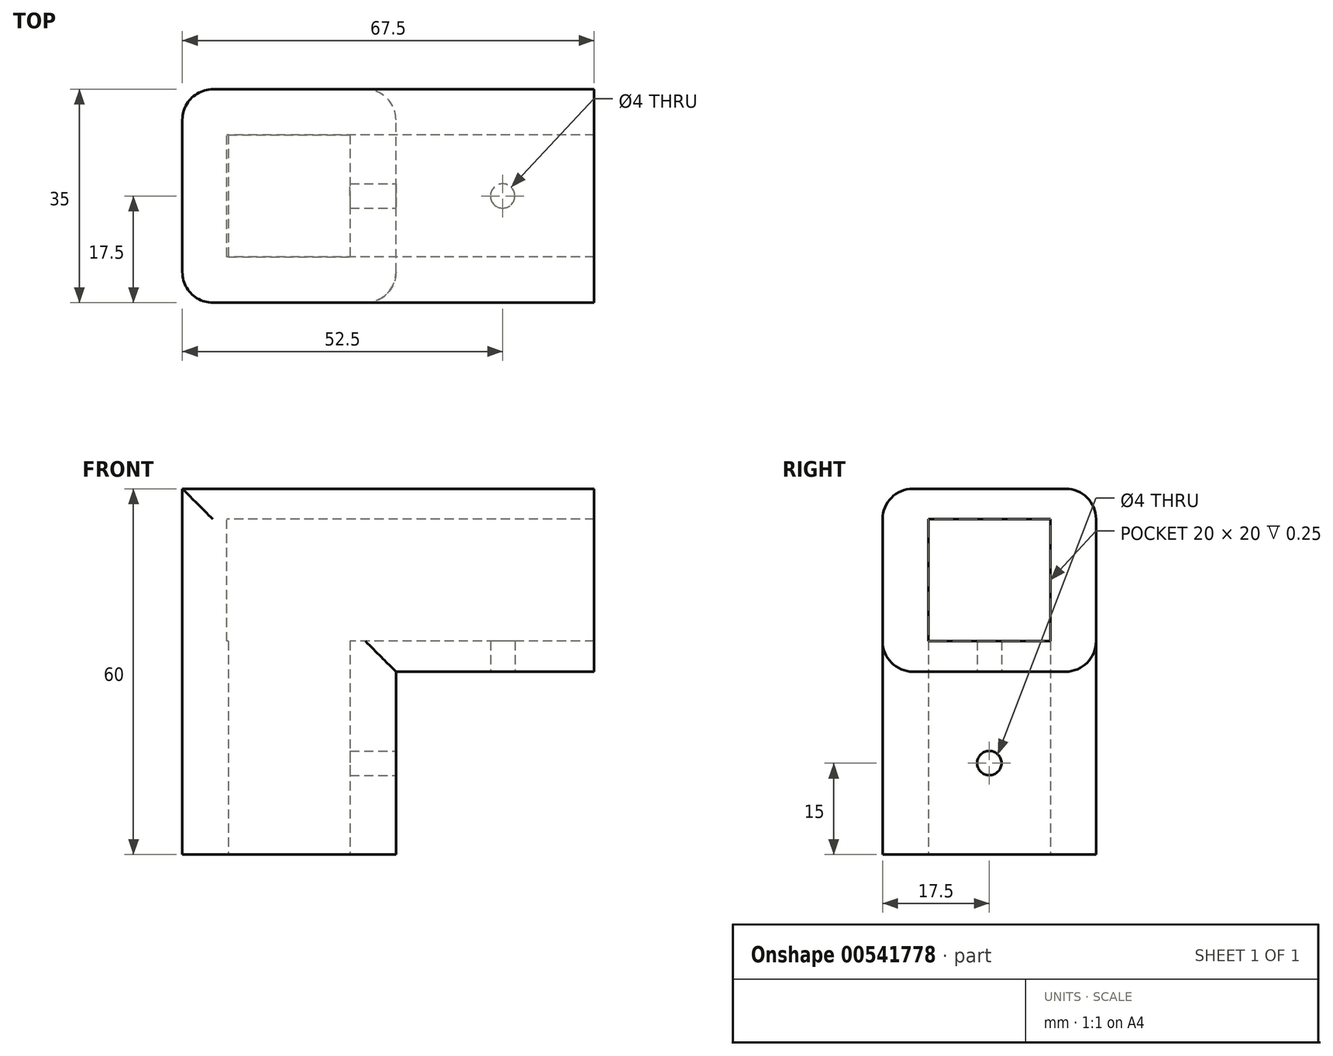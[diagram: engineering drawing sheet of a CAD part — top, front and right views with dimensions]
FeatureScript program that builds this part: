
annotation { "Feature Type Name" : "Feature", "Feature Type Description" : "" }
export const myFeature = defineFeature(function(context is Context, id is Id, definition is map)
    precondition{}
    {
        {
            var Q0;
            Q0=qCreatedBy(makeId("Top.planeOp"),FACE);
            var sketch = newSketch(context, id + "F0", { "sketchPlane" : qUnion([Q0])});
            skLineSegment(sketch, "E0.bottom", {"start": v(-17.5, -17.5) * mm, "end": v(17.5, -17.5) * mm});
            skLineSegment(sketch, "E0.top", {"start": v(-17.5, 17.5) * mm, "end": v(17.5, 17.5) * mm});
            skLineSegment(sketch, "E0.left", {"start": v(-17.5, -17.5) * mm, "end": v(-17.5, 17.5) * mm});
            skLineSegment(sketch, "E0.right", {"start": v(17.5, -17.5) * mm, "end": v(17.5, 17.5) * mm});
            skLineSegment(sketch, "E1.bottom", {"start": v(-10, -10) * mm, "end": v(10, -10) * mm});
            skLineSegment(sketch, "E1.top", {"start": v(-10, 10) * mm, "end": v(10, 10) * mm});
            skLineSegment(sketch, "E1.left", {"start": v(-10, -10) * mm, "end": v(-10, 10) * mm});
            skLineSegment(sketch, "E1.right", {"start": v(10, -10) * mm, "end": v(10, 10) * mm});
            skPoint(sketch, "E2", {"position": v(0, 10) * mm});
            skPoint(sketch, "E3", {"position": v(0, 17.5) * mm});
            skPoint(sketch, "E4", {"position": v(-17.5, 0) * mm});
            skPoint(sketch, "E5", {"position": v(-10, 0) * mm});
            skSolve(sketch);
        }
        {
            var Q0;
            Q0=makeQuery(id+"F0.imprint","IMPRINT",FACE,{"disambiguationData":[TD([[makeQuery(id+"F0.imprint","IMPRINT",EDGE,{"derivedFrom":sQuery(id+"F0.wireOp",EDGE,"E0.bottom")}),1.0]])]});
            extrude(context, id + "F1", {"entities" : qUnion([Q0]), "depth" : 60 * mm, "offsetDistance" : 25 * mm});
        }
        {
            var Q0;
            Q0=makeQuery(id+"F1.opExtrude","SWEPT_EDGE",EDGE,{"disambiguationData":[OSD([sQuery(id+"F0.wireOp",EDGE,"E0.top"),sQuery(id+"F0.wireOp",EDGE,"E0.right")])]});
            var Q1;
            Q1=makeQuery(id+"F1.opExtrude","SWEPT_EDGE",EDGE,{"disambiguationData":[OSD([sQuery(id+"F0.wireOp",EDGE,"E0.top"),sQuery(id+"F0.wireOp",EDGE,"E0.left")])]});
            var Q2;
            Q2=makeQuery(id+"F1.opExtrude","SWEPT_EDGE",EDGE,{"disambiguationData":[OSD([sQuery(id+"F0.wireOp",EDGE,"E0.bottom"),sQuery(id+"F0.wireOp",EDGE,"E0.right")])]});
            var Q3;
            Q3=makeQuery(id+"F1.opExtrude","SWEPT_EDGE",EDGE,{"disambiguationData":[OSD([sQuery(id+"F0.wireOp",EDGE,"E0.bottom"),sQuery(id+"F0.wireOp",EDGE,"E0.left")])]});
            fillet(context, id + "F2", {"entities" : qUnion([Q0, Q1, Q2, Q3]), "radius" : 5 * mm, "tangentPropagation" : true, "allowEdgeOverflow" : false});
        }
        {
            var Q0;
            Q0=makeQuery(id+"F1.opExtrude","SWEPT_FACE",FACE,{"disambiguationData":[OSD([sQuery(id+"F0.wireOp",EDGE,"E0.right")])]});
            var sketch = newSketch(context, id + "F3", { "sketchPlane" : qUnion([Q0])});
            skCircle(sketch, "E6", {"center": v(0, 40) * mm, "radius": 2 * mm});
            skCircle(sketch, "E7", {"center": v(0, 15) * mm, "radius": 2 * mm});
            skSolve(sketch);
        }
        {
            var Q0;
            Q0=qSketchRegion(id+"F3",true);
            extrude(context, id + "F4", {"entities" : qUnion([Q0]), "operationType" : NewBodyOperationType.REMOVE, "oppositeDirection" : true, "depth" : 10 * mm, "offsetDistance" : 25 * mm});
        }
        {
            var Q0;
            Q0=makeQuery(id+"F1.opExtrude","CAP_FACE",FACE,{"disambiguationData":[OSD([sQuery(id+"F0.wireOp",EDGE,"E0.bottom"),sQuery(id+"F0.wireOp",EDGE,"E0.top"),sQuery(id+"F0.wireOp",EDGE,"E0.left"),sQuery(id+"F0.wireOp",EDGE,"E0.right"),sQuery(id+"F0.wireOp",EDGE,"E1.bottom"),sQuery(id+"F0.wireOp",EDGE,"E1.top"),sQuery(id+"F0.wireOp",EDGE,"E1.left"),sQuery(id+"F0.wireOp",EDGE,"E1.right")])],"isStart":false});
            var sketch = newSketch(context, id + "F5", { "sketchPlane" : qUnion([Q0])});
            skLineSegment(sketch, "E8.bottom", {"start": v(-17.26, -17.5) * mm, "end": v(17.26, -17.5) * mm});
            skLineSegment(sketch, "E8.top", {"start": v(-17.26, 17.5) * mm, "end": v(17.26, 17.5) * mm});
            skLineSegment(sketch, "E8.left", {"start": v(-17.26, -17.5) * mm, "end": v(-17.26, 17.5) * mm});
            skLineSegment(sketch, "E8.right", {"start": v(17.26, -17.5) * mm, "end": v(17.26, 17.5) * mm});
            skLineSegment(sketch, "E9.bottom", {"start": v(10, 10) * mm, "end": v(-10, 10) * mm});
            skLineSegment(sketch, "E9.top", {"start": v(10, -10) * mm, "end": v(-10, -10) * mm});
            skLineSegment(sketch, "E9.left", {"start": v(10, 10) * mm, "end": v(10, -10) * mm});
            skLineSegment(sketch, "E9.right", {"start": v(-10, 10) * mm, "end": v(-10, -10) * mm});
            skPoint(sketch, "E10", {"position": v(-10, 0) * mm});
            skPoint(sketch, "E11", {"position": v(0, 10) * mm});
            skPoint(sketch, "E12", {"position": v(0, 17.5) * mm});
            skPoint(sketch, "E13", {"position": v(17.26, 0) * mm});
            skSolve(sketch);
        }
        {
            var Q0;
            Q0=qCreatedBy(makeId("Right.planeOp"),FACE);
            var sketch = newSketch(context, id + "F6", { "sketchPlane" : qUnion([Q0])});
            skLineSegment(sketch, "E14.bottom", {"start": v(-17.5, 60) * mm, "end": v(17.5, 60) * mm});
            skLineSegment(sketch, "E14.top", {"start": v(-17.5, 30) * mm, "end": v(17.5, 30) * mm});
            skLineSegment(sketch, "E14.left", {"start": v(-17.5, 60) * mm, "end": v(-17.5, 30) * mm});
            skLineSegment(sketch, "E14.right", {"start": v(17.5, 60) * mm, "end": v(17.5, 30) * mm});
            skPoint(sketch, "E15", {"position": v(0, 30) * mm});
            skPoint(sketch, "E16", {"position": v(17.5, 45) * mm});
            skLineSegment(sketch, "E17.bottom", {"start": v(-10, 35) * mm, "end": v(10, 35) * mm});
            skLineSegment(sketch, "E17.top", {"start": v(-10, 55) * mm, "end": v(10, 55) * mm});
            skLineSegment(sketch, "E17.left", {"start": v(-10, 35) * mm, "end": v(-10, 55) * mm});
            skLineSegment(sketch, "E17.right", {"start": v(10, 35) * mm, "end": v(10, 55) * mm});
            skPoint(sketch, "E18", {"position": v(0, 55) * mm});
            skPoint(sketch, "E19", {"position": v(10, 45) * mm});
            skSolve(sketch);
        }
        {
            var Q0;
            Q0=makeQuery(id+"F6.imprint","IMPRINT",FACE,{"disambiguationData":[TD([[makeQuery(id+"F6.imprint","IMPRINT",EDGE,{"derivedFrom":sQuery(id+"F6.wireOp",EDGE,"E17.bottom")}),1.0]])]});
            var Q1;
            Q1=makeQuery(id+"F6.imprint","IMPRINT",FACE,{"disambiguationData":[TD([[makeQuery(id+"F6.imprint","IMPRINT",EDGE,{"derivedFrom":sQuery(id+"F6.wireOp",EDGE,"E14.bottom")}),-1.0]])]});
            extrude(context, id + "F7", {"entities" : qUnion([Q0, Q1]), "operationType" : NewBodyOperationType.ADD, "depth" : 50 * mm, "offsetDistance" : 25 * mm});
        }
        {
            var Q0;
            Q0=makeQuery(id+"F6.imprint","IMPRINT",FACE,{"disambiguationData":[TD([[makeQuery(id+"F6.imprint","IMPRINT",EDGE,{"derivedFrom":sQuery(id+"F6.wireOp",EDGE,"E17.bottom")}),1.0]])]});
            var Q1;
            Q1=makeQuery(id+"F6.imprint","IMPRINT",FACE,{"disambiguationData":[TD([[makeQuery(id+"F6.imprint","IMPRINT",EDGE,{"derivedFrom":sQuery(id+"F6.wireOp",EDGE,"E14.bottom")}),-1.0]])]});
            var Q2;
            Q2=makeQuery(id+"F1.opExtrude","SWEPT_FACE",FACE,{"disambiguationData":[OSD([sQuery(id+"F0.wireOp",EDGE,"E0.left")])]});
            extrude(context, id + "F8", {"entities" : qUnion([Q0, Q1]), "operationType" : NewBodyOperationType.ADD, "endBound" : BoundingType.UP_TO_SURFACE, "oppositeDirection" : true, "depth" : 25 * mm, "endBoundEntityFace" : qUnion([Q2]), "offsetDistance" : 25 * mm});
        }
        {
            var Q0;
            Q0=makeQuery(id+"F6.imprint","IMPRINT",FACE,{"disambiguationData":[TD([[makeQuery(id+"F6.imprint","IMPRINT",EDGE,{"derivedFrom":sQuery(id+"F6.wireOp",EDGE,"E17.bottom")}),1.0]])]});
            extrude(context, id + "F9", {"entities" : qUnion([Q0]), "operationType" : NewBodyOperationType.REMOVE, "depth" : 60 * mm, "offsetDistance" : 25 * mm});
        }
        {
            var Q0;
            Q0=makeQuery(id+"F6.imprint","IMPRINT",FACE,{"disambiguationData":[TD([[makeQuery(id+"F6.imprint","IMPRINT",EDGE,{"derivedFrom":sQuery(id+"F6.wireOp",EDGE,"E17.bottom")}),1.0]])]});
            extrude(context, id + "F10", {"entities" : qUnion([Q0]), "operationType" : NewBodyOperationType.REMOVE, "oppositeDirection" : true, "depth" : 10.25 * mm, "offsetDistance" : 25 * mm});
        }
        {
            var Q0;
            Q0=makeQuery(id+"F0.imprint","IMPRINT",FACE,{"disambiguationData":[TD([[makeQuery(id+"F0.imprint","IMPRINT",EDGE,{"derivedFrom":sQuery(id+"F0.wireOp",EDGE,"E1.bottom")}),1.0]])]});
            var Q1;
            {var subQ0=sQuery(id+"F6.wireOp",EDGE,"E17.top");Q1=makeQuery(id+"F10.boolean.opBoolean","MERGE",FACE,{"derivedFrom":[makeQuery(id+"F9.boolean.opBoolean","COPY",FACE,{"derivedFrom":makeQuery(id+"F9.opExtrude","SWEPT_FACE",FACE,{"disambiguationData":[OSD([subQ0])]})}),makeQuery(id+"F10.opExtrude","SWEPT_FACE",FACE,{"disambiguationData":[OSD([subQ0])]})]});}
            extrude(context, id + "F11", {"entities" : qUnion([Q0]), "operationType" : NewBodyOperationType.REMOVE, "endBound" : BoundingType.UP_TO_SURFACE, "depth" : 55 * mm, "endBoundEntityFace" : qUnion([Q1]), "offsetDistance" : 25 * mm});
        }
        {
            var Q0;
            Q0=makeQuery(id+"F8.opExtrude","CAP_EDGE",EDGE,{"disambiguationData":[OSD([sQuery(id+"F6.wireOp",EDGE,"E14.left")])],"isStart":false});
            var Q1;
            Q1=makeQuery(id+"F8.opExtrude","CAP_EDGE",EDGE,{"disambiguationData":[OSD([sQuery(id+"F6.wireOp",EDGE,"E14.right")])],"isStart":false});
            var Q2;
            Q2=makeQuery(id+"F7.opExtrude","SWEPT_EDGE",EDGE,{"disambiguationData":[OSD([sQuery(id+"F6.wireOp",EDGE,"E14.top"),sQuery(id+"F6.wireOp",EDGE,"E14.left")])]});
            var Q3;
            Q3=makeQuery(id+"F7.opExtrude","SWEPT_EDGE",EDGE,{"disambiguationData":[OSD([sQuery(id+"F6.wireOp",EDGE,"E14.top"),sQuery(id+"F6.wireOp",EDGE,"E14.right")])]});
            var Q4;
            {var subQ0=sQuery(id+"F6.wireOp",EDGE,"E14.right");var subQ1=sQuery(id+"F6.wireOp",EDGE,"E14.bottom");Q4=makeQuery(id+"F8.boolean.opBoolean","MERGE",EDGE,{"derivedFrom":[makeQuery(id+"F7.boolean.opBoolean","MERGE",EDGE,{"derivedFrom":[makeQuery(id+"F1.opExtrude","CAP_EDGE",EDGE,{"disambiguationData":[OSD([sQuery(id+"F0.wireOp",EDGE,"E0.top")])],"isStart":false}),makeQuery(id+"F7.opExtrude","SWEPT_EDGE",EDGE,{"disambiguationData":[OSD([subQ1,subQ0])]})]}),makeQuery(id+"F8.opExtrude","SWEPT_EDGE",EDGE,{"disambiguationData":[OSD([subQ1,subQ0])]})]});}
            var Q5;
            {var subQ0=sQuery(id+"F6.wireOp",EDGE,"E14.left");var subQ1=sQuery(id+"F6.wireOp",EDGE,"E14.bottom");Q5=makeQuery(id+"F8.boolean.opBoolean","MERGE",EDGE,{"derivedFrom":[makeQuery(id+"F7.boolean.opBoolean","MERGE",EDGE,{"derivedFrom":[makeQuery(id+"F1.opExtrude","CAP_EDGE",EDGE,{"disambiguationData":[OSD([sQuery(id+"F0.wireOp",EDGE,"E0.bottom")])],"isStart":false}),makeQuery(id+"F7.opExtrude","SWEPT_EDGE",EDGE,{"disambiguationData":[OSD([subQ1,subQ0])]})]}),makeQuery(id+"F8.opExtrude","SWEPT_EDGE",EDGE,{"disambiguationData":[OSD([subQ1,subQ0])]})]});}
            fillet(context, id + "F12", {"entities" : qUnion([Q0, Q1, Q2, Q3, Q4, Q5]), "radius" : 5 * mm, "tangentPropagation" : true, "allowEdgeOverflow" : false});
        }
        {
            var Q0;
            {var subQ1=sQuery(id+"F0.wireOp",EDGE,"E0.bottom");var subQ5=sQuery(id+"F6.wireOp",EDGE,"E14.top");Q0=makeQuery(id+"F7.boolean.opBoolean","SPLIT",FACE,{"disambiguationData":[TD([makeQuery(id+"F1.opExtrude","SWEPT_FACE",FACE,{"disambiguationData":[OSD([subQ1])]})])],"derivedFrom":makeQuery(id+"F7.opExtrude","SWEPT_FACE",FACE,{"disambiguationData":[OSD([subQ5])]})});}
            var sketch = newSketch(context, id + "F13", { "sketchPlane" : qUnion([Q0])});
            skCircle(sketch, "E20", {"center": v(35, 0) * mm, "radius": 2 * mm});
            skSolve(sketch);
        }
        {
            var Q0;
            Q0=makeQuery(id+"F13.imprint","IMPRINT",FACE,{"disambiguationData":[TD([[makeQuery(id+"F13.imprint","IMPRINT",EDGE,{"derivedFrom":sQuery(id+"F13.wireOp",EDGE,"E20")}),1.0]])]});
            extrude(context, id + "F14", {"entities" : qUnion([Q0]), "operationType" : NewBodyOperationType.REMOVE, "oppositeDirection" : true, "depth" : 20 * mm, "offsetDistance" : 25 * mm});
        }
    });
